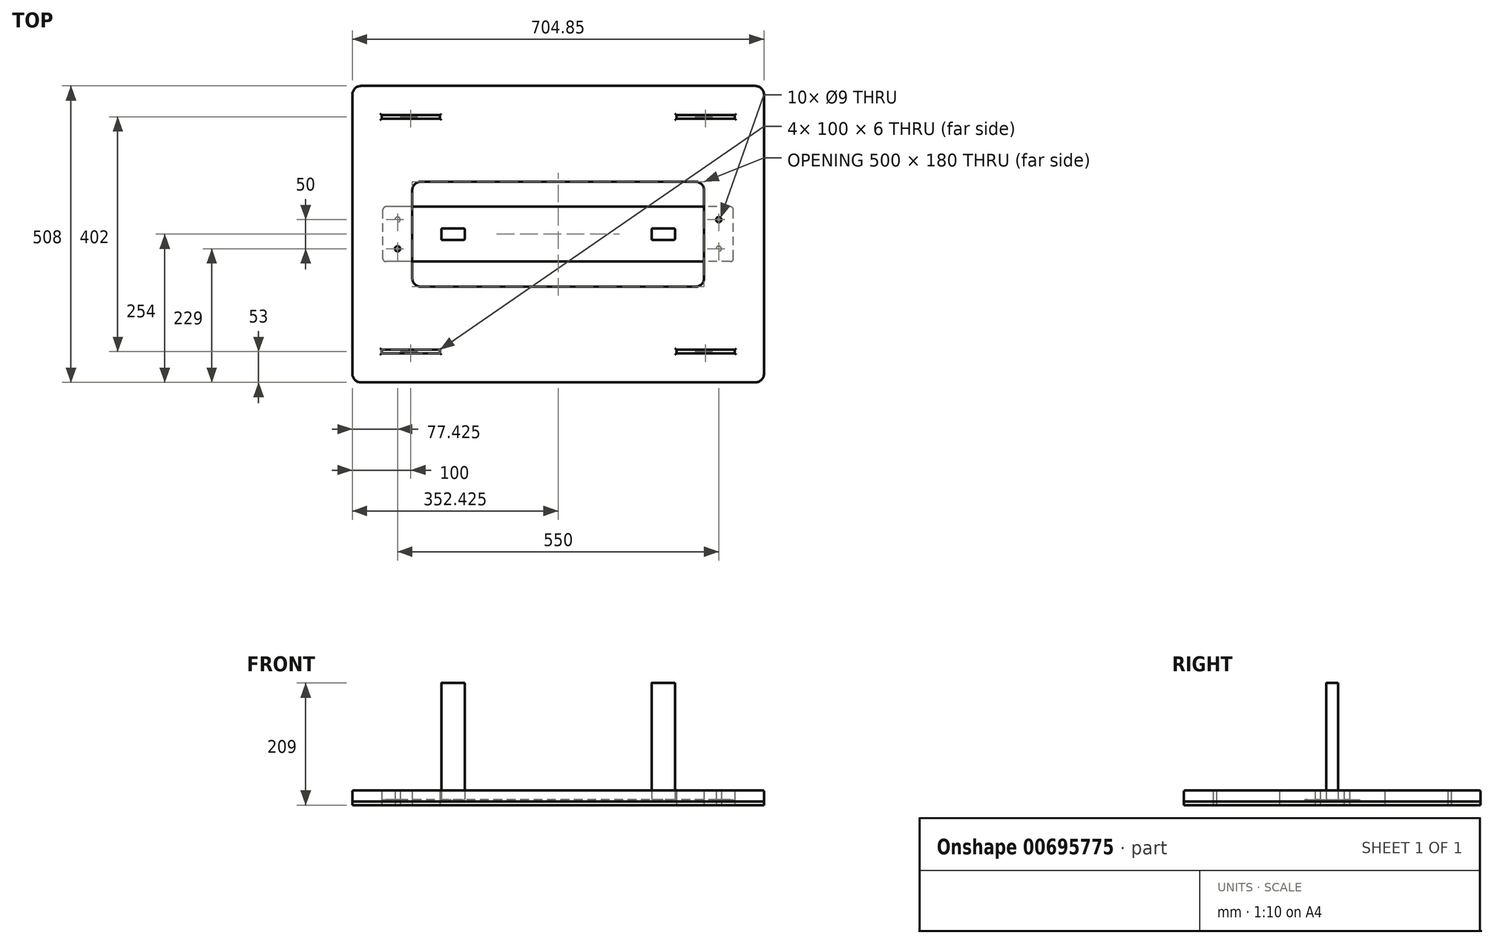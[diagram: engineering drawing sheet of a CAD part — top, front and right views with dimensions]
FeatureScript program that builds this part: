
annotation { "Feature Type Name" : "Feature", "Feature Type Description" : "" }
export const myFeature = defineFeature(function(context is Context, id is Id, definition is map)
    precondition{}
    {
        {
            var Q0;
            Q0=qCreatedBy(makeId("Top.planeOp"),FACE);
            var sketch = newSketch(context, id + "F0", { "sketchPlane" : qUnion([Q0])});
            skLineSegment(sketch, "E0.bottom", {"start": v(-15, 0) * mm, "end": v(-689.85, 0) * mm});
            skLineSegment(sketch, "E0.top", {"start": v(-15, 508) * mm, "end": v(-689.85, 508) * mm});
            skLineSegment(sketch, "E0.left", {"start": v(0, 15) * mm, "end": v(0, 493) * mm});
            skLineSegment(sketch, "E0.right", {"start": v(-704.85, 15) * mm, "end": v(-704.85, 493) * mm});
            skPoint(sketch, "E1.visualSharp", {"position": v(-704.85, 508) * mm});
            skArc(sketch, "E1.filletArc", {"start": v(-689.85, 508) * mm, "mid": v(-700.46, 503.6) * mm, "end": v(-704.85, 493) * mm});
            skPoint(sketch, "E2.visualSharp", {"position": v(-704.85, 0) * mm});
            skArc(sketch, "E2.filletArc", {"start": v(-704.85, 15) * mm, "mid": v(-700.46, 4.4) * mm, "end": v(-689.85, 0) * mm});
            skPoint(sketch, "E3.visualSharp", {"position": v(0, 508) * mm});
            skArc(sketch, "E3.filletArc", {"start": v(0, 493) * mm, "mid": v(-4.4, 503.6) * mm, "end": v(-15, 508) * mm});
            skPoint(sketch, "E4.visualSharp", {"position": v(0, 0) * mm});
            skArc(sketch, "E4.filletArc", {"start": v(-15, 0) * mm, "mid": v(-4.4, 4.4) * mm, "end": v(0, 15) * mm});
            skPoint(sketch, "E5.startSnap0", {"position": v(-352.43, 508) * mm});
            skPoint(sketch, "E6.startSnap0", {"position": v(-704.85, 254) * mm});
            skLineSegment(sketch, "E7.bottom", {"start": v(-117.43, 164) * mm, "end": v(-587.43, 164) * mm});
            skLineSegment(sketch, "E7.top", {"start": v(-117.43, 344) * mm, "end": v(-587.43, 344) * mm});
            skLineSegment(sketch, "E7.left", {"start": v(-102.43, 179) * mm, "end": v(-102.43, 329) * mm});
            skLineSegment(sketch, "E7.right", {"start": v(-602.43, 179) * mm, "end": v(-602.43, 329) * mm});
            skPoint(sketch, "E7.middle", {"position": v(-352.43, 254) * mm});
            skPoint(sketch, "E8.visualSharp", {"position": v(-602.42, 344) * mm});
            skArc(sketch, "E8.filletArc", {"start": v(-587.43, 344) * mm, "mid": v(-598.03, 339.6) * mm, "end": v(-602.43, 329) * mm});
            skPoint(sketch, "E9.visualSharp", {"position": v(-602.43, 164) * mm});
            skArc(sketch, "E9.filletArc", {"start": v(-602.43, 179) * mm, "mid": v(-598.03, 168.4) * mm, "end": v(-587.43, 164) * mm});
            skPoint(sketch, "E10.visualSharp", {"position": v(-102.43, 344) * mm});
            skArc(sketch, "E10.filletArc", {"start": v(-102.43, 329) * mm, "mid": v(-106.82, 339.6) * mm, "end": v(-117.43, 344) * mm});
            skPoint(sketch, "E11.visualSharp", {"position": v(-102.43, 164) * mm});
            skArc(sketch, "E11.filletArc", {"start": v(-117.43, 164) * mm, "mid": v(-106.82, 168.4) * mm, "end": v(-102.43, 179) * mm});
            skCircle(sketch, "E12", {"center": v(-627.43, 279) * mm, "radius": 4.5 * mm});
            skCircle(sketch, "E13.MirrorC", {"center": v(-627.43, 229) * mm, "radius": 4.5 * mm});
            skCircle(sketch, "E14.MirrorC", {"center": v(-77.42, 279) * mm, "radius": 4.5 * mm});
            skCircle(sketch, "E15.MirrorC", {"center": v(-77.42, 229) * mm, "radius": 4.5 * mm});
            skLineSegment(sketch, "E16.bottom", {"start": v(-654.85, 458) * mm, "end": v(-554.85, 458) * mm});
            skLineSegment(sketch, "E16.top", {"start": v(-654.85, 452) * mm, "end": v(-554.85, 452) * mm});
            skLineSegment(sketch, "E16.left", {"start": v(-654.85, 458) * mm, "end": v(-654.85, 452) * mm});
            skLineSegment(sketch, "E16.right", {"start": v(-554.85, 458) * mm, "end": v(-554.85, 452) * mm});
            skLineSegment(sketch, "E17.MirrorCS", {"start": v(-50, 458) * mm, "end": v(-150, 458) * mm});
            skLineSegment(sketch, "E18.MirrorCS", {"start": v(-150, 458) * mm, "end": v(-150, 452) * mm});
            skLineSegment(sketch, "E19.MirrorCS", {"start": v(-50, 452) * mm, "end": v(-150, 452) * mm});
            skLineSegment(sketch, "E20.MirrorCS", {"start": v(-50, 458) * mm, "end": v(-50, 452) * mm});
            skLineSegment(sketch, "E21.MirrorCS", {"start": v(-50, 56) * mm, "end": v(-150, 56) * mm});
            skLineSegment(sketch, "E22.MirrorCS", {"start": v(-150, 50) * mm, "end": v(-150, 56) * mm});
            skLineSegment(sketch, "E23.MirrorCS", {"start": v(-50, 50) * mm, "end": v(-150, 50) * mm});
            skLineSegment(sketch, "E24.MirrorCS", {"start": v(-50, 50) * mm, "end": v(-50, 56) * mm});
            skLineSegment(sketch, "E25.MirrorCS", {"start": v(-654.85, 50) * mm, "end": v(-554.85, 50) * mm});
            skLineSegment(sketch, "E26.MirrorCS", {"start": v(-554.85, 50) * mm, "end": v(-554.85, 56) * mm});
            skLineSegment(sketch, "E27.MirrorCS", {"start": v(-654.85, 56) * mm, "end": v(-554.85, 56) * mm});
            skLineSegment(sketch, "E28.MirrorCS", {"start": v(-654.85, 50) * mm, "end": v(-654.85, 56) * mm});
            skSolve(sketch);
        }
        {
            var Q0;
            Q0=makeQuery(id+"F0.imprint","IMPRINT",FACE,{"disambiguationData":[TD([[makeQuery(id+"F0.imprint","IMPRINT",EDGE,{"derivedFrom":sQuery(id+"F0.wireOp",EDGE,"E0.bottom")}),-1.0]])]});
            extrude(context, id + "F1", {"entities" : qUnion([Q0]), "depth" : 6 * mm, "offsetDistance" : 25 * mm});
        }
        {
            var Q0;
            Q0=makeQuery(id+"F1.opExtrude","CAP_FACE",FACE,{"disambiguationData":[OSD([sQuery(id+"F0.wireOp",EDGE,"E0.bottom"),sQuery(id+"F0.wireOp",EDGE,"E0.top"),sQuery(id+"F0.wireOp",EDGE,"E0.left"),sQuery(id+"F0.wireOp",EDGE,"E0.right"),sQuery(id+"F0.wireOp",EDGE,"E1.filletArc"),sQuery(id+"F0.wireOp",EDGE,"E2.filletArc"),sQuery(id+"F0.wireOp",EDGE,"E3.filletArc"),sQuery(id+"F0.wireOp",EDGE,"E4.filletArc"),sQuery(id+"F0.wireOp",EDGE,"E7.bottom"),sQuery(id+"F0.wireOp",EDGE,"E7.top"),sQuery(id+"F0.wireOp",EDGE,"E7.left"),sQuery(id+"F0.wireOp",EDGE,"E7.right"),sQuery(id+"F0.wireOp",EDGE,"E8.filletArc"),sQuery(id+"F0.wireOp",EDGE,"E9.filletArc"),sQuery(id+"F0.wireOp",EDGE,"E10.filletArc"),sQuery(id+"F0.wireOp",EDGE,"E11.filletArc"),sQuery(id+"F0.wireOp",EDGE,"E12"),sQuery(id+"F0.wireOp",EDGE,"E13.MirrorC"),sQuery(id+"F0.wireOp",EDGE,"E14.MirrorC"),sQuery(id+"F0.wireOp",EDGE,"E15.MirrorC"),sQuery(id+"F0.wireOp",EDGE,"E16.bottom"),sQuery(id+"F0.wireOp",EDGE,"E16.top"),sQuery(id+"F0.wireOp",EDGE,"E16.left"),sQuery(id+"F0.wireOp",EDGE,"E16.right"),sQuery(id+"F0.wireOp",EDGE,"E17.MirrorCS"),sQuery(id+"F0.wireOp",EDGE,"E18.MirrorCS"),sQuery(id+"F0.wireOp",EDGE,"E19.MirrorCS"),sQuery(id+"F0.wireOp",EDGE,"E20.MirrorCS"),sQuery(id+"F0.wireOp",EDGE,"E21.MirrorCS"),sQuery(id+"F0.wireOp",EDGE,"E22.MirrorCS"),sQuery(id+"F0.wireOp",EDGE,"E23.MirrorCS"),sQuery(id+"F0.wireOp",EDGE,"E24.MirrorCS"),sQuery(id+"F0.wireOp",EDGE,"E25.MirrorCS"),sQuery(id+"F0.wireOp",EDGE,"E26.MirrorCS"),sQuery(id+"F0.wireOp",EDGE,"E27.MirrorCS"),sQuery(id+"F0.wireOp",EDGE,"E28.MirrorCS")])],"isStart":true});
            var sketch = newSketch(context, id + "F2", { "sketchPlane" : qUnion([Q0])});
            skCircle(sketch, "E29.0", {"center": v(-627.43, -229) * mm, "radius": 4.5 * mm});
            skCircle(sketch, "E30.MirrorC", {"center": v(-627.43, -279) * mm, "radius": 4.5 * mm});
            skCircle(sketch, "E31.MirrorC", {"center": v(-77.42, -229) * mm, "radius": 4.5 * mm});
            skCircle(sketch, "E32.MirrorC", {"center": v(-77.42, -279) * mm, "radius": 4.5 * mm});
            skSolve(sketch);
        }
        {
            var Q0;
            Q0=makeQuery(id+"F2.imprint","IMPRINT",FACE,{"disambiguationData":[TD([[makeQuery(id+"F2.imprint","IMPRINT",EDGE,{"derivedFrom":sQuery(id+"F2.wireOp",EDGE,"E30.MirrorC")}),-1.0]])]});
            var Q1;
            Q1=makeQuery(id+"F2.imprint","IMPRINT",FACE,{"disambiguationData":[TD([[makeQuery(id+"F2.imprint","IMPRINT",EDGE,{"derivedFrom":sQuery(id+"F2.wireOp",EDGE,"E29.0")}),1.0]])]});
            var Q2;
            Q2=makeQuery(id+"F2.imprint","IMPRINT",FACE,{"disambiguationData":[TD([[makeQuery(id+"F2.imprint","IMPRINT",EDGE,{"derivedFrom":sQuery(id+"F2.wireOp",EDGE,"E32.MirrorC")}),1.0]])]});
            var Q3;
            Q3=makeQuery(id+"F2.imprint","IMPRINT",FACE,{"disambiguationData":[TD([[makeQuery(id+"F2.imprint","IMPRINT",EDGE,{"derivedFrom":sQuery(id+"F2.wireOp",EDGE,"E31.MirrorC")}),-1.0]])]});
            extrude(context, id + "F3", {"entities" : qUnion([Q0, Q1, Q2, Q3]), "oppositeDirection" : true, "depth" : 25 * mm, "offsetDistance" : 25 * mm});
        }
        {
            var Q0;
            Q0=makeQuery(id+"F3.opExtrude","CAP_FACE",FACE,{"disambiguationData":[OSD([sQuery(id+"F2.wireOp",EDGE,"E30.MirrorC")])],"isStart":false});
            var Q1;
            Q1=makeQuery(id+"F3.opExtrude","CAP_FACE",FACE,{"disambiguationData":[OSD([sQuery(id+"F2.wireOp",EDGE,"E29.0")])],"isStart":false});
            var Q2;
            Q2=makeQuery(id+"F3.opExtrude","CAP_FACE",FACE,{"disambiguationData":[OSD([sQuery(id+"F2.wireOp",EDGE,"E32.MirrorC")])],"isStart":false});
            var Q3;
            Q3=makeQuery(id+"F3.opExtrude","CAP_FACE",FACE,{"disambiguationData":[OSD([sQuery(id+"F2.wireOp",EDGE,"E31.MirrorC")])],"isStart":false});
            fillet(context, id + "F4", {"entities" : qUnion([Q0, Q1, Q2, Q3]), "radius" : 2 * mm, "tangentPropagation" : true, "allowEdgeOverflow" : false});
        }
        {
            var Q0;
            Q0=makeQuery(id+"F1.opExtrude","CAP_FACE",FACE,{"disambiguationData":[OSD([sQuery(id+"F0.wireOp",EDGE,"E0.bottom"),sQuery(id+"F0.wireOp",EDGE,"E0.top"),sQuery(id+"F0.wireOp",EDGE,"E0.left"),sQuery(id+"F0.wireOp",EDGE,"E0.right"),sQuery(id+"F0.wireOp",EDGE,"E1.filletArc"),sQuery(id+"F0.wireOp",EDGE,"E2.filletArc"),sQuery(id+"F0.wireOp",EDGE,"E3.filletArc"),sQuery(id+"F0.wireOp",EDGE,"E4.filletArc"),sQuery(id+"F0.wireOp",EDGE,"E7.bottom"),sQuery(id+"F0.wireOp",EDGE,"E7.top"),sQuery(id+"F0.wireOp",EDGE,"E7.left"),sQuery(id+"F0.wireOp",EDGE,"E7.right"),sQuery(id+"F0.wireOp",EDGE,"E8.filletArc"),sQuery(id+"F0.wireOp",EDGE,"E9.filletArc"),sQuery(id+"F0.wireOp",EDGE,"E10.filletArc"),sQuery(id+"F0.wireOp",EDGE,"E11.filletArc"),sQuery(id+"F0.wireOp",EDGE,"E12"),sQuery(id+"F0.wireOp",EDGE,"E13.MirrorC"),sQuery(id+"F0.wireOp",EDGE,"E14.MirrorC"),sQuery(id+"F0.wireOp",EDGE,"E15.MirrorC"),sQuery(id+"F0.wireOp",EDGE,"E16.bottom"),sQuery(id+"F0.wireOp",EDGE,"E16.top"),sQuery(id+"F0.wireOp",EDGE,"E16.left"),sQuery(id+"F0.wireOp",EDGE,"E16.right"),sQuery(id+"F0.wireOp",EDGE,"E17.MirrorCS"),sQuery(id+"F0.wireOp",EDGE,"E18.MirrorCS"),sQuery(id+"F0.wireOp",EDGE,"E19.MirrorCS"),sQuery(id+"F0.wireOp",EDGE,"E20.MirrorCS"),sQuery(id+"F0.wireOp",EDGE,"E21.MirrorCS"),sQuery(id+"F0.wireOp",EDGE,"E22.MirrorCS"),sQuery(id+"F0.wireOp",EDGE,"E23.MirrorCS"),sQuery(id+"F0.wireOp",EDGE,"E24.MirrorCS"),sQuery(id+"F0.wireOp",EDGE,"E25.MirrorCS"),sQuery(id+"F0.wireOp",EDGE,"E26.MirrorCS"),sQuery(id+"F0.wireOp",EDGE,"E27.MirrorCS"),sQuery(id+"F0.wireOp",EDGE,"E28.MirrorCS")])],"isStart":false});
            var sketch = newSketch(context, id + "F5", { "sketchPlane" : qUnion([Q0])});
            skLineSegment(sketch, "E33.0", {"start": v(-352.43, 599.99) * mm, "end": v(-352.43, -115.63) * mm});
            skLineSegment(sketch, "E34.0", {"start": v(-895.9, 254) * mm, "end": v(114.24, 254) * mm});
            skLineSegment(sketch, "E35.bottom", {"start": v(-57.43, 207.02) * mm, "end": v(-647.43, 207.02) * mm});
            skLineSegment(sketch, "E35.top", {"start": v(-57.43, 300.98) * mm, "end": v(-647.43, 300.98) * mm});
            skLineSegment(sketch, "E35.left", {"start": v(-52.43, 212.02) * mm, "end": v(-52.43, 295.98) * mm});
            skLineSegment(sketch, "E35.right", {"start": v(-652.43, 212.02) * mm, "end": v(-652.43, 295.98) * mm});
            skPoint(sketch, "E35.middle", {"position": v(-352.43, 254) * mm});
            skPoint(sketch, "E36.visualSharp", {"position": v(-652.43, 300.98) * mm});
            skArc(sketch, "E36.filletArc", {"start": v(-647.43, 300.98) * mm, "mid": v(-650.96, 299.52) * mm, "end": v(-652.43, 295.98) * mm});
            skPoint(sketch, "E37.visualSharp", {"position": v(-652.43, 207.02) * mm});
            skArc(sketch, "E37.filletArc", {"start": v(-652.43, 212.02) * mm, "mid": v(-650.96, 208.48) * mm, "end": v(-647.43, 207.02) * mm});
            skPoint(sketch, "E38.visualSharp", {"position": v(-52.43, 300.98) * mm});
            skArc(sketch, "E38.filletArc", {"start": v(-52.43, 295.98) * mm, "mid": v(-53.89, 299.52) * mm, "end": v(-57.43, 300.98) * mm});
            skPoint(sketch, "E39.visualSharp", {"position": v(-52.43, 207.02) * mm});
            skArc(sketch, "E39.filletArc", {"start": v(-57.43, 207.02) * mm, "mid": v(-53.89, 208.48) * mm, "end": v(-52.43, 212.02) * mm});
            skCircle(sketch, "E40", {"center": v(-627.43, 279) * mm, "radius": 4.5 * mm});
            skCircle(sketch, "E41.MirrorC", {"center": v(-627.43, 229) * mm, "radius": 4.5 * mm});
            skCircle(sketch, "E42.MirrorC", {"center": v(-77.42, 279) * mm, "radius": 4.5 * mm});
            skCircle(sketch, "E43.MirrorC", {"center": v(-77.42, 229) * mm, "radius": 4.5 * mm});
            skSolve(sketch);
        }
        {
            var Q0;
            {var subQ0=sQuery(id+"F5.wireOp",EDGE,"E36.filletArc");Q0=makeQuery(id+"F5.imprint","IMPRINT",FACE,{"disambiguationData":[TD([[makeQuery(id+"F5.imprint","IMPRINT",EDGE,{"derivedFrom":subQ0}),1.0]])]});}
            var Q1;
            {var subQ0=sQuery(id+"F5.wireOp",EDGE,"E35.top");var subQ1=sQuery(id+"F5.wireOp",EDGE,"E33.0");var subQ2=makeQuery(id+"F5.imprint","INTERSECT",VERTEX,{"derivedFrom":[subQ1,subQ0]});Q1=makeQuery(id+"F5.imprint","IMPRINT",FACE,{"disambiguationData":[TD([[makeQuery(id+"F5.imprint","IMPRINT",EDGE,{"disambiguationData":[TD([[subQ2,-1.0]])],"derivedFrom":subQ1}),-1.0]])]});}
            var Q2;
            {var subQ0=sQuery(id+"F5.wireOp",EDGE,"E37.filletArc");Q2=makeQuery(id+"F5.imprint","IMPRINT",FACE,{"disambiguationData":[TD([[makeQuery(id+"F5.imprint","IMPRINT",EDGE,{"derivedFrom":subQ0}),1.0]])]});}
            var Q3;
            {var subQ0=sQuery(id+"F5.wireOp",EDGE,"E34.0");var subQ1=sQuery(id+"F5.wireOp",EDGE,"E33.0");var subQ2=makeQuery(id+"F5.imprint","INTERSECT",VERTEX,{"derivedFrom":[subQ1,subQ0]});Q3=makeQuery(id+"F5.imprint","IMPRINT",FACE,{"disambiguationData":[TD([[makeQuery(id+"F5.imprint","IMPRINT",EDGE,{"disambiguationData":[TD([[subQ2,-1.0]])],"derivedFrom":subQ1}),-1.0]])]});}
            var Q4;
            {var subQ0=sQuery(id+"F5.wireOp",EDGE,"E34.0");var subQ1=sQuery(id+"F5.wireOp",EDGE,"E33.0");var subQ2=makeQuery(id+"F5.imprint","INTERSECT",VERTEX,{"derivedFrom":[subQ1,subQ0]});Q4=makeQuery(id+"F5.imprint","IMPRINT",FACE,{"disambiguationData":[TD([[makeQuery(id+"F5.imprint","IMPRINT",EDGE,{"disambiguationData":[TD([[subQ2,-1.0]])],"derivedFrom":subQ1}),1.0]])]});}
            var Q5;
            {var subQ0=sQuery(id+"F5.wireOp",EDGE,"E35.top");var subQ1=sQuery(id+"F5.wireOp",EDGE,"E33.0");var subQ2=makeQuery(id+"F5.imprint","INTERSECT",VERTEX,{"derivedFrom":[subQ1,subQ0]});Q5=makeQuery(id+"F5.imprint","IMPRINT",FACE,{"disambiguationData":[TD([[makeQuery(id+"F5.imprint","IMPRINT",EDGE,{"disambiguationData":[TD([[subQ2,-1.0]])],"derivedFrom":subQ1}),1.0]])]});}
            var Q6;
            {var subQ0=sQuery(id+"F5.wireOp",EDGE,"E38.filletArc");Q6=makeQuery(id+"F5.imprint","IMPRINT",FACE,{"disambiguationData":[TD([[makeQuery(id+"F5.imprint","IMPRINT",EDGE,{"derivedFrom":subQ0}),1.0]])]});}
            var Q7;
            {var subQ0=sQuery(id+"F5.wireOp",EDGE,"E39.filletArc");Q7=makeQuery(id+"F5.imprint","IMPRINT",FACE,{"disambiguationData":[TD([[makeQuery(id+"F5.imprint","IMPRINT",EDGE,{"derivedFrom":subQ0}),1.0]])]});}
            extrude(context, id + "F6", {"entities" : qUnion([Q0, Q1, Q2, Q3, Q4, Q5, Q6, Q7]), "depth" : 3 * mm, "offsetDistance" : 25 * mm});
        }
        {
            var Q0;
            Q0=makeQuery(id+"F6.opExtrude","CAP_FACE",FACE,{"disambiguationData":[OSD([sQuery(id+"F5.wireOp",EDGE,"E35.bottom"),sQuery(id+"F5.wireOp",EDGE,"E35.top"),sQuery(id+"F5.wireOp",EDGE,"E35.left"),sQuery(id+"F5.wireOp",EDGE,"E35.right"),sQuery(id+"F5.wireOp",EDGE,"E36.filletArc"),sQuery(id+"F5.wireOp",EDGE,"E37.filletArc"),sQuery(id+"F5.wireOp",EDGE,"E38.filletArc"),sQuery(id+"F5.wireOp",EDGE,"E39.filletArc"),sQuery(id+"F5.wireOp",EDGE,"E40"),sQuery(id+"F5.wireOp",EDGE,"E41.MirrorC"),sQuery(id+"F5.wireOp",EDGE,"E42.MirrorC"),sQuery(id+"F5.wireOp",EDGE,"E43.MirrorC")])],"isStart":false});
            var sketch = newSketch(context, id + "F7", { "sketchPlane" : qUnion([Q0])});
            skLineSegment(sketch, "E44", {"start": v(-552.43, 254) * mm, "end": v(-552.43, 262) * mm});
            skLineSegment(sketch, "E45", {"start": v(-550.43, 264) * mm, "end": v(-514.43, 264) * mm});
            skLineSegment(sketch, "E46", {"start": v(-512.43, 262) * mm, "end": v(-512.43, 254) * mm});
            skLineSegment(sketch, "E47.MirrorCS", {"start": v(-512.43, 246) * mm, "end": v(-512.43, 254) * mm});
            skLineSegment(sketch, "E48.MirrorCS", {"start": v(-550.43, 244) * mm, "end": v(-514.43, 244) * mm});
            skLineSegment(sketch, "E49.MirrorCS", {"start": v(-552.43, 254) * mm, "end": v(-552.43, 246) * mm});
            skLineSegment(sketch, "E50.MirrorCS", {"start": v(-192.43, 262) * mm, "end": v(-192.43, 254) * mm});
            skLineSegment(sketch, "E51.MirrorCS", {"start": v(-154.43, 264) * mm, "end": v(-190.43, 264) * mm});
            skLineSegment(sketch, "E52.MirrorCS", {"start": v(-152.43, 254) * mm, "end": v(-152.43, 262) * mm});
            skLineSegment(sketch, "E53.MirrorCS", {"start": v(-152.43, 254) * mm, "end": v(-152.43, 246) * mm});
            skLineSegment(sketch, "E54.MirrorCS", {"start": v(-154.43, 244) * mm, "end": v(-190.43, 244) * mm});
            skLineSegment(sketch, "E55.MirrorCS", {"start": v(-192.43, 246) * mm, "end": v(-192.43, 254) * mm});
            skPoint(sketch, "E56.visualSharp", {"position": v(-512.43, 264) * mm});
            skArc(sketch, "E56.filletArc", {"start": v(-512.43, 262) * mm, "mid": v(-513.01, 263.41) * mm, "end": v(-514.43, 264) * mm});
            skPoint(sketch, "E57.visualSharp", {"position": v(-512.43, 244) * mm});
            skArc(sketch, "E57.filletArc", {"start": v(-514.43, 244) * mm, "mid": v(-513.01, 244.59) * mm, "end": v(-512.43, 246) * mm});
            skPoint(sketch, "E58.visualSharp", {"position": v(-552.43, 244) * mm});
            skArc(sketch, "E58.filletArc", {"start": v(-552.43, 246) * mm, "mid": v(-551.84, 244.59) * mm, "end": v(-550.43, 244) * mm});
            skPoint(sketch, "E59.visualSharp", {"position": v(-552.43, 264) * mm});
            skArc(sketch, "E59.filletArc", {"start": v(-550.43, 264) * mm, "mid": v(-551.84, 263.41) * mm, "end": v(-552.43, 262) * mm});
            skPoint(sketch, "E60.visualSharp", {"position": v(-192.43, 264) * mm});
            skArc(sketch, "E60.filletArc", {"start": v(-190.43, 264) * mm, "mid": v(-191.84, 263.41) * mm, "end": v(-192.43, 262) * mm});
            skPoint(sketch, "E61.visualSharp", {"position": v(-192.43, 244) * mm});
            skArc(sketch, "E61.filletArc", {"start": v(-192.43, 246) * mm, "mid": v(-191.84, 244.59) * mm, "end": v(-190.43, 244) * mm});
            skPoint(sketch, "E62.visualSharp", {"position": v(-152.43, 244) * mm});
            skArc(sketch, "E62.filletArc", {"start": v(-154.43, 244) * mm, "mid": v(-153.01, 244.59) * mm, "end": v(-152.43, 246) * mm});
            skPoint(sketch, "E63.visualSharp", {"position": v(-152.43, 264) * mm});
            skArc(sketch, "E63.filletArc", {"start": v(-152.43, 262) * mm, "mid": v(-153.01, 263.41) * mm, "end": v(-154.43, 264) * mm});
            skSolve(sketch);
        }
        {
            var Q0;
            Q0=makeQuery(id+"F7.imprint","IMPRINT",FACE,{"disambiguationData":[TD([[makeQuery(id+"F7.imprint","IMPRINT",EDGE,{"derivedFrom":sQuery(id+"F7.wireOp",EDGE,"E44")}),-1.0]])]});
            var Q1;
            Q1=makeQuery(id+"F7.imprint","IMPRINT",FACE,{"disambiguationData":[TD([[makeQuery(id+"F7.imprint","IMPRINT",EDGE,{"derivedFrom":sQuery(id+"F7.wireOp",EDGE,"E50.MirrorCS")}),1.0]])]});
            extrude(context, id + "F8", {"entities" : qUnion([Q0, Q1]), "depth" : 200 * mm, "offsetDistance" : 25 * mm});
        }
    });
